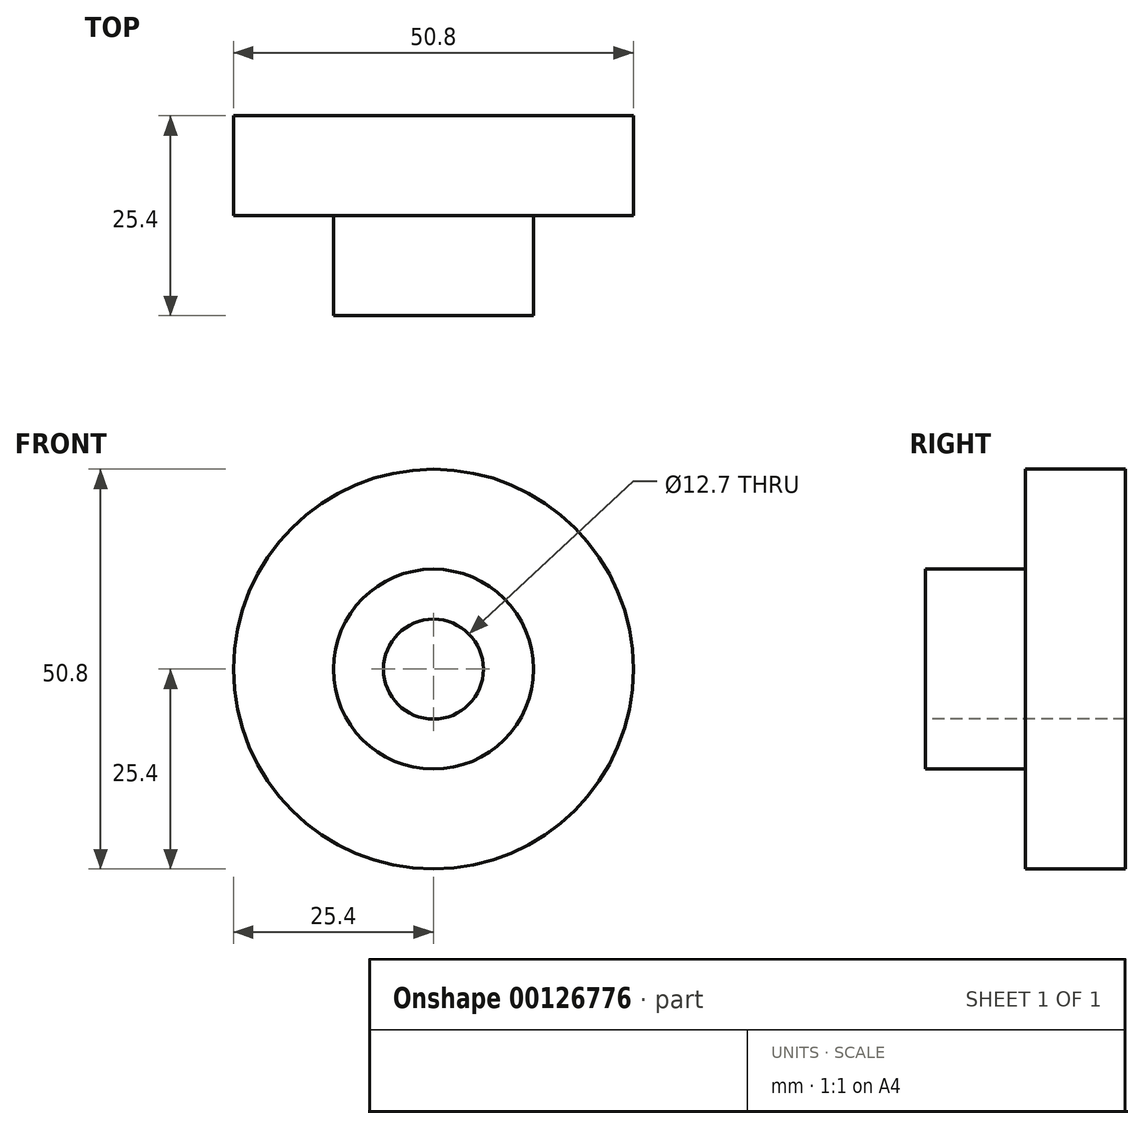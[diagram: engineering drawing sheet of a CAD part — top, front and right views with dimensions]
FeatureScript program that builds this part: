
annotation { "Feature Type Name" : "Feature", "Feature Type Description" : "" }
export const myFeature = defineFeature(function(context is Context, id is Id, definition is map)
    precondition{}
    {
        {
            var Q0;
            Q0=qCreatedBy(makeId("Front.planeOp"),FACE);
            var sketch = newSketch(context, id + "F0", { "sketchPlane" : qUnion([Q0])});
            skCircle(sketch, "E0", {"center": v(0, 0) * mm, "radius": 25.4 * mm});
            skSolve(sketch);
        }
        {
            var Q0;
            Q0 = qSketchRegion(id + "F0", true);
            extrude(context, id + "F1", {"entities" : qUnion([Q0]), "depth" : 12.7 * mm});
        }
        {
            var Q0;
            Q0=makeQuery(id+"F1.opExtrude","CAP_FACE",FACE,{"disambiguationData":[OSD([sQuery(id+"F0.wireOp",EDGE,"E0")])],"isStart":false});
            var sketch = newSketch(context, id + "F2", { "sketchPlane" : qUnion([Q0])});
            skCircle(sketch, "E1", {"center": v(0, 0) * mm, "radius": 12.7 * mm});
            skSolve(sketch);
        }
        {
            var Q0;
            Q0=makeQuery(id+"F2.imprint","IMPRINT",FACE,{"disambiguationData":[TD([[makeQuery(id+"F2.imprint","IMPRINT",EDGE,{"derivedFrom":sQuery(id+"F2.wireOp",EDGE,"E1")}),1.0]])]});
            extrude(context, id + "F3", {"entities" : qUnion([Q0]), "operationType" : NewBodyOperationType.ADD, "depth" : 12.7 * mm});
        }
        {
            var Q0;
            Q0=makeQuery(id+"F3.opExtrude","CAP_FACE",FACE,{"disambiguationData":[OSD([sQuery(id+"F2.wireOp",EDGE,"E1")])],"isStart":false});
            var sketch = newSketch(context, id + "F4", { "sketchPlane" : qUnion([Q0])});
            skCircle(sketch, "E2", {"center": v(0, 0) * mm, "radius": 6.35 * mm});
            skSolve(sketch);
        }
        {
            var Q0;
            Q0=makeQuery(id+"F4.imprint","IMPRINT",FACE,{"disambiguationData":[TD([[makeQuery(id+"F4.imprint","IMPRINT",EDGE,{"derivedFrom":sQuery(id+"F4.wireOp",EDGE,"E2")}),1.0]])]});
            var Q1;
            Q1=makeQuery(id+"F1.opExtrude","CAP_FACE",FACE,{"disambiguationData":[OSD([sQuery(id+"F0.wireOp",EDGE,"E0")])],"isStart":true});
            extrude(context, id + "F5", {"entities" : qUnion([Q0]), "operationType" : NewBodyOperationType.REMOVE, "endBound" : BoundingType.UP_TO_SURFACE, "oppositeDirection" : true, "endBoundEntityFace" : qUnion([Q1]), "depth" : 25.4 * mm});
        }
    });
